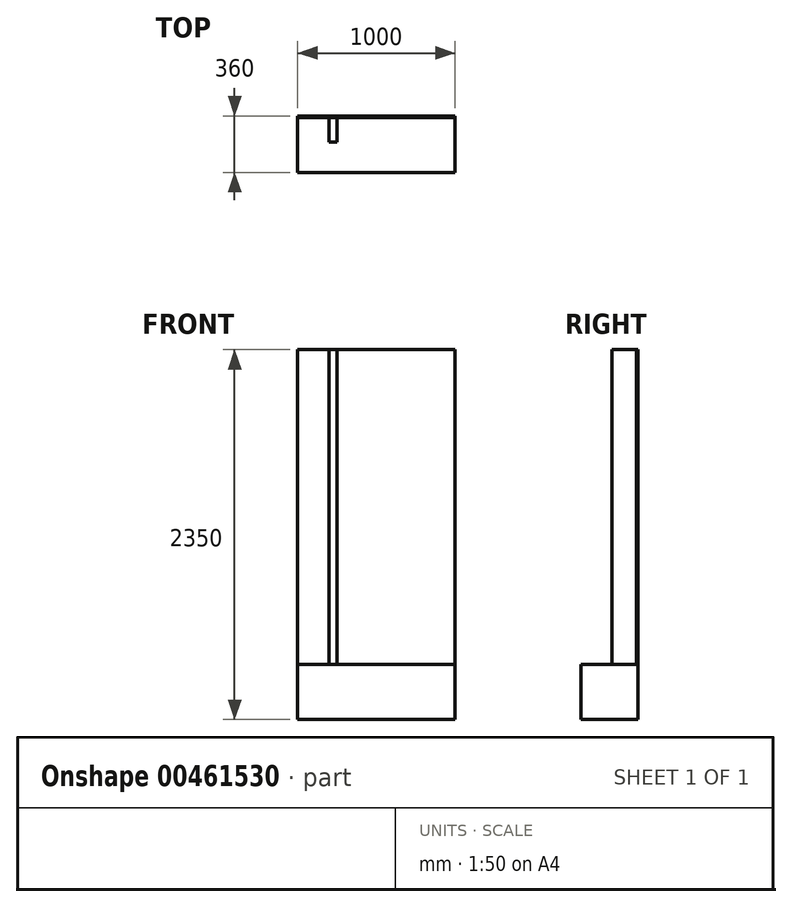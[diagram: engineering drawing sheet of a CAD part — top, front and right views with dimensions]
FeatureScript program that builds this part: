
annotation { "Feature Type Name" : "Feature", "Feature Type Description" : "" }
export const myFeature = defineFeature(function(context is Context, id is Id, definition is map)
    precondition{}
    {
        {
            assignVariable(context, id + "F0", {"name" : "stepHeight", "anyValue" : 350});
        }
        {
            var Q0;
            Q0=qCreatedBy(makeId("Top.planeOp"),FACE);
            var sketch = newSketch(context, id + "F1", { "sketchPlane" : qUnion([Q0])});
            skLineSegment(sketch, "E0.bottom", {"start": v(-452, 392.62) * mm, "end": v(548, 392.62) * mm});
            skLineSegment(sketch, "E0.top", {"start": v(-452, 382.62) * mm, "end": v(548, 382.62) * mm});
            skLineSegment(sketch, "E0.left", {"start": v(-452, 392.62) * mm, "end": v(-452, 382.62) * mm});
            skLineSegment(sketch, "E0.right", {"start": v(548, 392.62) * mm, "end": v(548, 382.62) * mm});
            skLineSegment(sketch, "E1.bottom", {"start": v(-252, 382.62) * mm, "end": v(-201.5, 382.62) * mm});
            skLineSegment(sketch, "E1.top", {"start": v(-252, 227.62) * mm, "end": v(-201.5, 227.62) * mm});
            skLineSegment(sketch, "E1.left", {"start": v(-252, 382.62) * mm, "end": v(-252, 227.62) * mm});
            skLineSegment(sketch, "E1.right", {"start": v(-201.5, 382.62) * mm, "end": v(-201.5, 227.62) * mm});
            skLineSegment(sketch, "E2.top", {"start": v(-452, 32.62) * mm, "end": v(548, 32.62) * mm});
            skLineSegment(sketch, "E2.left", {"start": v(-452, 382.62) * mm, "end": v(-452, 32.62) * mm});
            skLineSegment(sketch, "E2.right", {"start": v(548, 382.62) * mm, "end": v(548, 32.62) * mm});
            skSolve(sketch);
        }
        {
            var Q0;
            Q0=makeQuery(id+"F1.imprint","IMPRINT",FACE,{"disambiguationData":[TD([[makeQuery(id+"F1.imprint","IMPRINT",EDGE,{"derivedFrom":sQuery(id+"F1.wireOp",EDGE,"E0.bottom")}),-1.0]])]});
            extrude(context, id + "F2", {"entities" : qUnion([Q0]), "depth" : 2000 * mm});
        }
        {
            var Q0;
            Q0=makeQuery(id+"F1.imprint","IMPRINT",FACE,{"disambiguationData":[TD([[makeQuery(id+"F1.imprint","IMPRINT",EDGE,{"derivedFrom":sQuery(id+"F1.wireOp",EDGE,"E1.top")}),1.0]])]});
            extrude(context, id + "F3", {"entities" : qUnion([Q0]), "depth" : 2000 * mm});
        }
        {
            var Q0;
            Q0=makeQuery(id+"F1.imprint","IMPRINT",FACE,{"disambiguationData":[TD([[makeQuery(id+"F1.imprint","IMPRINT",EDGE,{"derivedFrom":sQuery(id+"F1.wireOp",EDGE,"E1.top")}),-1.0]])]});
            var Q1;
            Q1=makeQuery(id+"F1.imprint","IMPRINT",FACE,{"disambiguationData":[TD([[makeQuery(id+"F1.imprint","IMPRINT",EDGE,{"derivedFrom":sQuery(id+"F1.wireOp",EDGE,"E1.top")}),1.0]])]});
            var Q2;
            Q2=makeQuery(id+"F1.imprint","IMPRINT",FACE,{"disambiguationData":[TD([[makeQuery(id+"F1.imprint","IMPRINT",EDGE,{"derivedFrom":sQuery(id+"F1.wireOp",EDGE,"E0.bottom")}),-1.0]])]});
            extrude(context, id + "F4", {"entities" : qUnion([Q0, Q1, Q2]), "oppositeDirection" : true, "depth" : (getVariable(context, 'stepHeight')) * mm});
        }
    });
